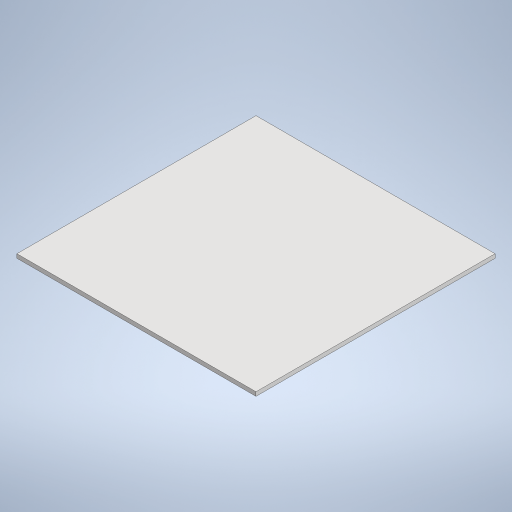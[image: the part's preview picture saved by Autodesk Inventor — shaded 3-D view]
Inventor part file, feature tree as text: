
AUTODESK INVENTOR PART (.ipt)
format: ipt  version: 2024 (Build 280153000, 153)  size: 201,216 bytes
history: native  units: mm
features: extrude x1, sketch x1
ambient origin geometry x8: Origin, YZ Plane, XZ Plane, XY Plane, X Axis, Y Axis, Z Axis, Center Point
bodies: Solid1 (feature_tree)
feature tree (2):
  extrude  "Extrusion1"  Depth=300.0mm
  sketch  "Sketch1"  dims[d0=300.0mm d1=300.0mm d2=5.0mm d3=0.0mm]
